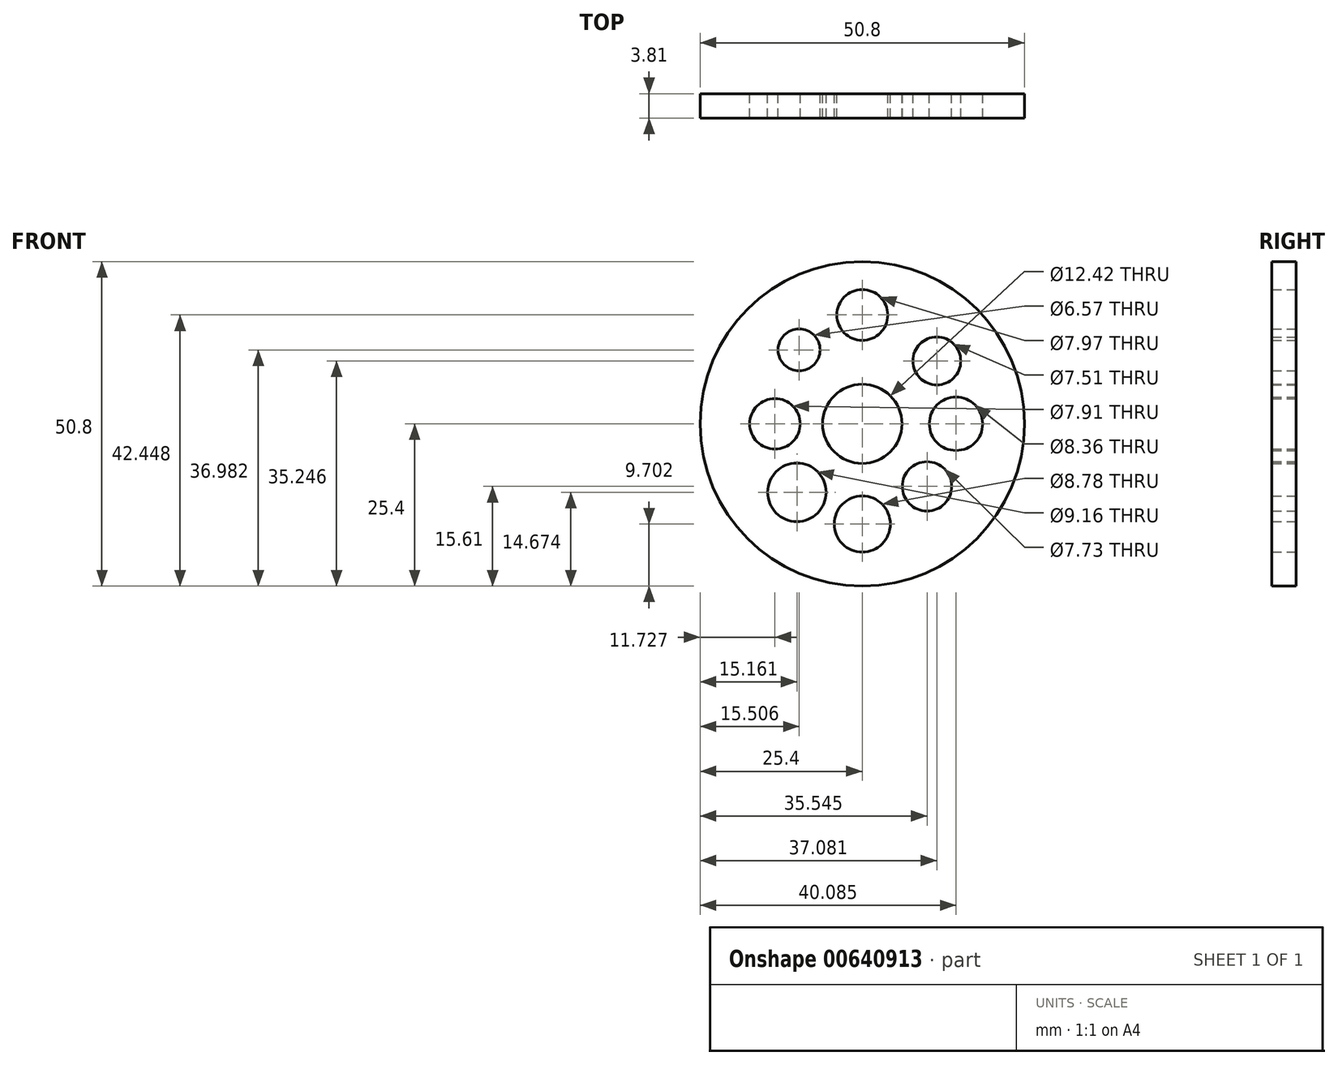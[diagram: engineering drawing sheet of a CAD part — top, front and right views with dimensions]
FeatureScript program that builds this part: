
annotation { "Feature Type Name" : "Feature", "Feature Type Description" : "" }
export const myFeature = defineFeature(function(context is Context, id is Id, definition is map)
    precondition{}
    {
        {
            var Q0;
            Q0=qCreatedBy(makeId("Front.planeOp"),FACE);
            var sketch = newSketch(context, id + "F0", { "sketchPlane" : qUnion([Q0])});
            skCircle(sketch, "E0", {"center": v(0, 0) * mm, "radius": 25.4 * mm});
            skCircle(sketch, "E1", {"center": v(0, 0) * mm, "radius": 6.21 * mm});
            skCircle(sketch, "E2", {"center": v(-9.9, 11.58) * mm, "radius": 3.29 * mm});
            skPoint(sketch, "E2.first.point", {"position": v(-13, 12.66) * mm});
            skPoint(sketch, "E2.second.point", {"position": v(-7.93, 8.95) * mm});
            skPoint(sketch, "E2.third.point", {"position": v(-7.26, 9.62) * mm});
            skCircle(sketch, "E3", {"center": v(0, 17.05) * mm, "radius": 3.98 * mm});
            skCircle(sketch, "E4", {"center": v(11.68, 9.85) * mm, "radius": 3.75 * mm});
            skPoint(sketch, "E4.first.point", {"position": v(10.3, 13.34) * mm});
            skPoint(sketch, "E4.second.point", {"position": v(14.69, 7.6) * mm});
            skPoint(sketch, "E4.third.point", {"position": v(7.93, 9.62) * mm});
            skCircle(sketch, "E5", {"center": v(-13.67, 0) * mm, "radius": 3.96 * mm});
            skCircle(sketch, "E6", {"center": v(14.69, 0) * mm, "radius": 4.18 * mm});
            skCircle(sketch, "E7", {"center": v(0, -15.7) * mm, "radius": 4.4 * mm});
            skCircle(sketch, "E8", {"center": v(-10.24, -10.73) * mm, "radius": 4.58 * mm});
            skPoint(sketch, "E8.first.point", {"position": v(-14.69, -9.62) * mm});
            skPoint(sketch, "E8.second.point", {"position": v(-7.93, -14.69) * mm});
            skPoint(sketch, "E8.third.point", {"position": v(-9.28, -6.25) * mm});
            skCircle(sketch, "E9", {"center": v(10.14, -9.8) * mm, "radius": 3.86 * mm});
            skPoint(sketch, "E9.first.point", {"position": v(11.68, -13.34) * mm});
            skPoint(sketch, "E9.second.point", {"position": v(8.6, -6.25) * mm});
            skPoint(sketch, "E9.third.point", {"position": v(11.68, -6.25) * mm});
            skSolve(sketch);
        }
        {
            var Q0;
            Q0=makeQuery(id+"F0.imprint","IMPRINT",FACE,{"disambiguationData":[TD([[makeQuery(id+"F0.imprint","IMPRINT",EDGE,{"derivedFrom":sQuery(id+"F0.wireOp",EDGE,"E0")}),1.0]])]});
            extrude(context, id + "F1", {"entities" : qUnion([Q0]), "depth" : 3.8 * mm, "offsetDistance" : 25.4 * mm});
        }
    });
